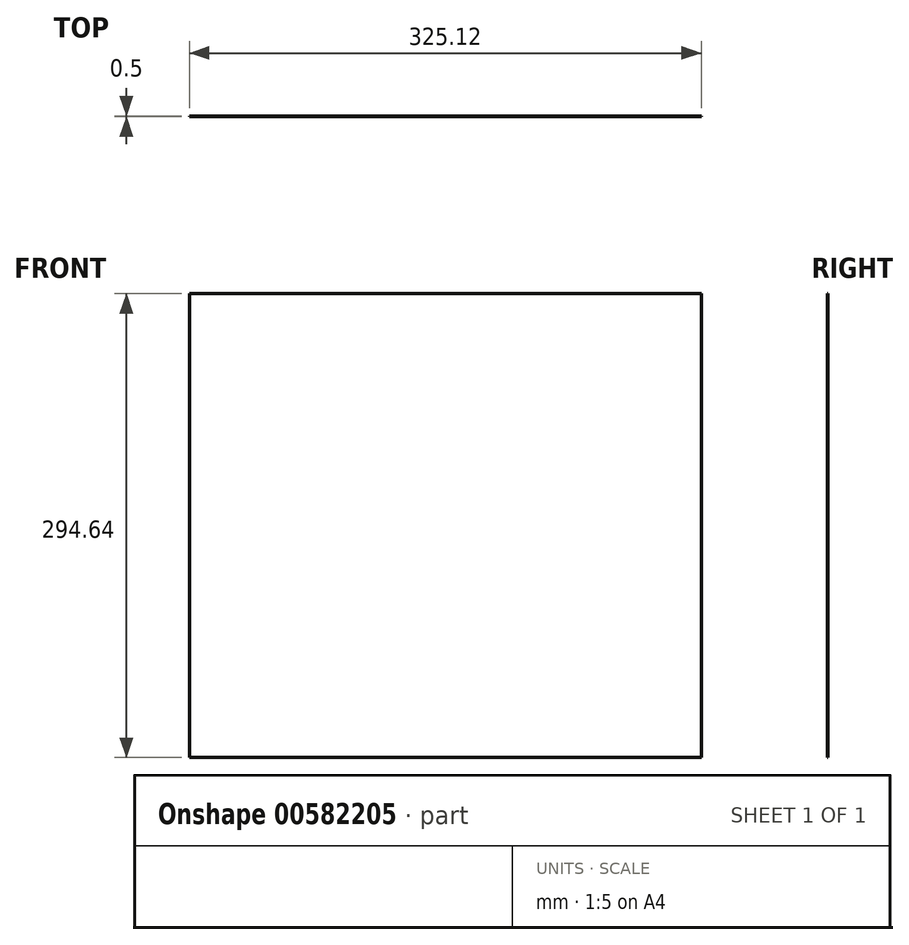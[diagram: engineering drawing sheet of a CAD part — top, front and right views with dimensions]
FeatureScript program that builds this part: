
annotation { "Feature Type Name" : "Feature", "Feature Type Description" : "" }
export const myFeature = defineFeature(function(context is Context, id is Id, definition is map)
    precondition{}
    {
        {
            var Q0;
            Q0=qCreatedBy(makeId("Front.planeOp"),FACE);
            var sketch = newSketch(context, id + "F0", { "sketchPlane" : qUnion([Q0])});
            skLineSegment(sketch, "E0.bottom", {"start": v(-160.31, 193.28) * mm, "end": v(164.8, 193.28) * mm});
            skLineSegment(sketch, "E0.top", {"start": v(-160.31, -101.36) * mm, "end": v(164.8, -101.36) * mm});
            skLineSegment(sketch, "E0.left", {"start": v(-160.31, 193.28) * mm, "end": v(-160.31, -101.36) * mm});
            skLineSegment(sketch, "E0.right", {"start": v(164.8, 193.28) * mm, "end": v(164.8, -101.36) * mm});
            skSolve(sketch);
        }
        {
            var Q0;
            Q0=makeQuery(id+"F0.imprint","IMPRINT",FACE,{"disambiguationData":[TD([[makeQuery(id+"F0.imprint","IMPRINT",EDGE,{"derivedFrom":sQuery(id+"F0.wireOp",EDGE,"E0.bottom")}),-1.0]])]});
            extrude(context, id + "F1", {"entities" : qUnion([Q0]), "depth" : 0.5 * mm, "offsetDistance" : 25 * mm});
        }
    });
